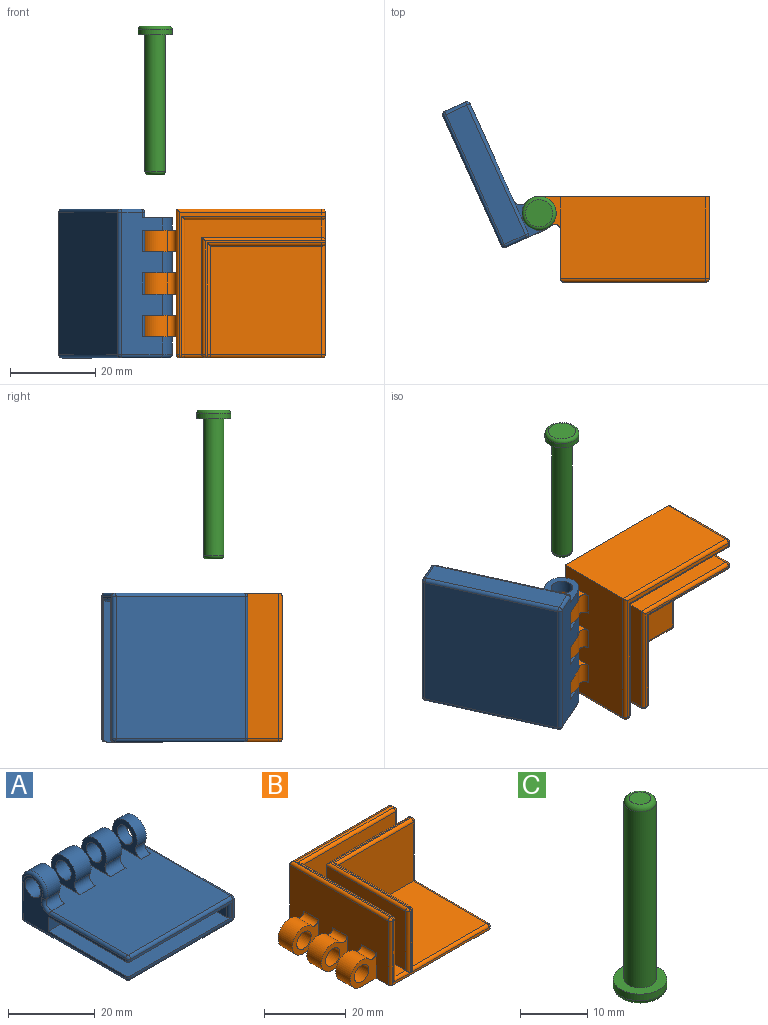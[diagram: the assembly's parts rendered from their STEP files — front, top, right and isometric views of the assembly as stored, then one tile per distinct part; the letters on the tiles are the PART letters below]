
ASSEMBLY  parts=3 mates=2
PART A: 55 faces, bbox 35x35.3x15.5 mm
  f0: plane 33.4x5.4mm, normal (1,0,0), area 180.4mm2, adj f42,f43,f47,f48
  f1: plane 33.4x10.4mm, normal (0,1,0), area 266.4mm2, adj f2,f3,f4,f5,f19,f20,f21,f23
  f2: cylinder r=4mm len=8mm, axis (1,0,0), area 71.1mm2, adj f1,f6,f23,f27
  f3: cylinder r=4mm len=8mm, axis (1,0,0), area 71.1mm2, adj f1,f7,f20,f24
  f4: cylinder r=4mm len=8mm, axis (1,0,0), area 42.7mm2, adj f1,f8,f19,f21
  f5: cylinder r=4mm len=8mm, axis (1,0,0), area 59.7mm2, adj f1,f9,f26,f30
  f6: cylinder r=1.84mm len=5mm, axis (1,0,0), area 18.3mm2, adj f2,f18,f23,f27
  f7: cylinder r=1.84mm len=5mm, axis (1,0,0), area 18.3mm2, adj f3,f18,f20,f24
  f8: cylinder r=1.84mm len=3mm, axis (1,0,0), area 11mm2, adj f4,f18,f19,f21
  f9: cylinder r=1.84mm len=4.2mm, axis (1,0,0), area 15.4mm2, adj f5,f18,f26,f32
  f10: cylinder r=2.5mm len=5mm, axis (1,0,0), area 78.5mm2, adj f12,f26
  f11: plane 33.8x26mm, normal (0,0,1), area 858mm2, adj f12,f13,f15,f16,f29,f54
  f12: plane 33.4x13.6mm, normal (-1,0,0), area 107.6mm2, adj f10,f11,f15,f17,f29,f30,f32,f33
  f13: plane 33.4x5.4mm, normal (0,-1,0), area 48.4mm2, adj f11,f17,f29,f35,f36,f43,f44,f54
  f14: plane 33.4x33.4mm, normal (0,0,-1), area 1115.6mm2, adj f34,f35,f41,f42
  f15: plane 33x4mm, normal (0,-1,0), area 132mm2, adj f11,f12,f16,f17
  f16: plane 25.2x4mm, normal (-1,0,0), area 100.8mm2, adj f11,f15,f17,f54
  f17: plane 33.8x26mm, normal (0,0,-1), area 858mm2, adj f12,f13,f15,f16,f36,f54
  f18: plane 33.4x33.4mm, normal (0,0,1), area 968.5mm2, adj f6,f7,f8,f9,f19,f20,f21,f23
  f19: plane 9.35x9mm, normal (1,0,0), area 38.5mm2, adj f1,f4,f8,f18,f28,f50
  f20: plane 9.35x9mm, normal (1,0,0), area 38.5mm2, adj f1,f3,f7,f18,f22,f51
  f21: plane 9.35x9mm, normal (-1,0,0), area 38.5mm2, adj f1,f4,f8,f18,f28,f51
  f22: cylinder r=2.5mm len=5mm, axis (1,0,0), area 78.5mm2, adj f20,f24
  f23: plane 9.35x9mm, normal (1,0,0), area 38.5mm2, adj f1,f2,f6,f18,f25,f52
  f24: plane 9.35x9mm, normal (-1,0,0), area 38.5mm2, adj f1,f3,f7,f18,f22,f52
  f25: cylinder r=2.5mm len=5mm, axis (1,0,0), area 78.5mm2, adj f23,f27
  f26: plane 9.35x9mm, normal (1,0,0), area 38.5mm2, adj f1,f5,f9,f10,f18,f53
  f27: plane 9.35x9mm, normal (-1,0,0), area 38.5mm2, adj f1,f2,f6,f18,f25,f53
  f28: cylinder r=2.5mm len=5mm, axis (1,0,0), area 47.1mm2, adj f19,f21
  f29: cylinder r=0.8mm len=0.8mm, axis (0,0,1), area 0.9mm2, adj f11,f12,f13,f31
  f30: torus R=3.2mm, axis (1,0,0), area 16.6mm2, adj f5,f12,f32,f33
  f31: sphere r=0.8mm, area 1mm2, adj f29,f34,f35
  f32: torus R=2.64mm, axis (1,0,0), area 5.3mm2, adj f9,f12,f30,f37
  f33: cylinder r=0.8mm len=10.4mm, axis (0,0,-1), area 13.1mm2, adj f1,f12,f30,f38
  f34: cylinder r=0.8mm len=33.4mm, axis (0,-1,0), area 42mm2, adj f12,f14,f31,f38
  f35: cylinder r=0.8mm len=33.4mm, axis (1,0,0), area 42mm2, adj f13,f14,f31,f39
  f36: cylinder r=0.8mm len=0.8mm, axis (0,0,1), area 0.9mm2, adj f12,f13,f17,f40
  f37: cylinder r=0.8mm len=24.85mm, axis (0,1,0), area 31.2mm2, adj f12,f18,f32,f40
  f38: sphere r=0.8mm, area 1mm2, adj f33,f34,f41
  f39: sphere r=0.8mm, area 1mm2, adj f35,f42,f43
  f40: sphere r=0.8mm, area 1mm2, adj f36,f37,f44
  f41: cylinder r=0.8mm len=33.4mm, axis (-1,0,0), area 42mm2, adj f1,f14,f38,f45
  f42: cylinder r=0.8mm len=33.4mm, axis (0,1,0), area 42mm2, adj f0,f14,f39,f45
  f43: cylinder r=0.8mm len=5.4mm, axis (0,0,-1), area 6.8mm2, adj f0,f13,f39,f46
  f44: cylinder r=0.8mm len=33.4mm, axis (-1,0,0), area 42mm2, adj f13,f18,f40,f46
  f45: sphere r=0.8mm, area 1mm2, adj f41,f42,f47
  f46: sphere r=0.8mm, area 1mm2, adj f43,f44,f48
  f47: cylinder r=0.8mm len=5.4mm, axis (0,0,1), area 6.8mm2, adj f0,f1,f45,f49
  f48: cylinder r=0.8mm len=33.4mm, axis (0,-1,0), area 42mm2, adj f0,f18,f46,f49
  f49: sphere r=0.8mm, area 1mm2, adj f47,f48,f50
  f50: cylinder r=0.8mm len=1.2mm, axis (1,0,0), area 1.5mm2, adj f1,f18,f19,f49
  f51: cylinder r=0.8mm len=5mm, axis (1,0,0), area 6.3mm2, adj f1,f18,f20,f21
  f52: cylinder r=0.8mm len=5mm, axis (1,0,0), area 6.3mm2, adj f1,f18,f23,f24
  f53: cylinder r=0.8mm len=5mm, axis (1,0,0), area 6.3mm2, adj f1,f18,f26,f27
  f54: cylinder r=0.8mm len=4mm, axis (0,0,1), area 5mm2, adj f11,f13,f16,f17
PART B: 64 faces, bbox 44x35x20 mm
  f0: plane 40.77x35mm, normal (0,0,-1), area 1311.2mm2, adj f4,f5,f6,f7,f9,f10,f11,f21
  f1: cylinder r=1.28mm len=5mm, axis (0,1,0), area 15mm2, adj f4,f7,f24,f26
  f2: cylinder r=1.28mm len=5mm, axis (0,1,0), area 15mm2, adj f5,f7,f22,f25
  f3: cylinder r=1.28mm len=5mm, axis (0,1,0), area 15mm2, adj f6,f7,f21,f23
  f4: cylinder r=4mm len=7.92mm, axis (0,1,0), area 74.6mm2, adj f0,f1,f24,f26
  f5: cylinder r=4mm len=7.92mm, axis (0,1,0), area 74.6mm2, adj f0,f2,f22,f25
  f6: cylinder r=4mm len=7.92mm, axis (0,1,0), area 74.6mm2, adj f0,f3,f21,f23
  f7: plane 34.2x19.2mm, normal (-1,0,0), area 541.7mm2, adj f0,f1,f2,f3,f11,f21,f22,f23
  f8: plane 32.2x31.7mm, normal (0,0,1), area 245.2mm2, adj f13,f14,f16,f17,f43,f47
  f9: plane 33.4x19.2mm, normal (0,-1,0), area 38.2mm2, adj f0,f30,f35,f41,f43,f45,f51,f57
  f10: plane 33.4x19.2mm, normal (1,0,0), area 47.4mm2, adj f0,f34,f40,f44,f47,f50,f56,f59
  f11: plane 34.2x19.2mm, normal (0,1,0), area 656.6mm2, adj f0,f7,f33,f34
  f12: plane 26.2x25.5mm, normal (0,0,1), area 668.1mm2, adj f18,f19,f60,f63
  f13: plane 31.7x17.7mm, normal (1,0,0), area 561.1mm2, adj f8,f14,f36,f41
  f14: plane 32.2x17.7mm, normal (0,-1,0), area 569.9mm2, adj f8,f13,f39,f44
  f15: plane 33.4x33.4mm, normal (0,0,1), area 43.1mm2, adj f31,f33,f35,f36,f39,f40
  f16: plane 28.2x17.7mm, normal (0,1,0), area 499.1mm2, adj f8,f17,f49,f50
  f17: plane 27.5x17.7mm, normal (-1,0,0), area 486.7mm2, adj f8,f16,f45,f46
  f18: plane 25.5x17.7mm, normal (1,0,0), area 451.3mm2, adj f12,f19,f52,f57
  f19: plane 26.2x17.7mm, normal (0,-1,0), area 463.7mm2, adj f12,f18,f55,f61
  f20: plane 27.4x26.7mm, normal (0,0,1), area 21.5mm2, adj f46,f49,f51,f52,f55,f56
  f21: plane 9x7.92mm, normal (0,-1,0), area 41.2mm2, adj f0,f3,f6,f7,f27
  f22: plane 9x7.92mm, normal (0,-1,0), area 41.2mm2, adj f0,f2,f5,f7,f28
  f23: plane 9x7.92mm, normal (0,1,0), area 41.2mm2, adj f0,f3,f6,f7,f27
  f24: plane 9x7.92mm, normal (0,-1,0), area 41.2mm2, adj f0,f1,f4,f7,f29
  f25: plane 9x7.92mm, normal (0,1,0), area 41.2mm2, adj f0,f2,f5,f7,f28
  f26: plane 9x7.92mm, normal (0,1,0), area 41.2mm2, adj f0,f1,f4,f7,f29
  f27: cylinder r=2.5mm len=5mm, axis (0,1,0), area 78.5mm2, adj f21,f23
  f28: cylinder r=2.5mm len=5mm, axis (0,1,0), area 78.5mm2, adj f22,f25
  f29: cylinder r=2.5mm len=5mm, axis (0,1,0), area 78.5mm2, adj f24,f26
  f30: cylinder r=0.8mm len=19.2mm, axis (0,0,-1), area 24.1mm2, adj f0,f7,f9,f32
  f31: cylinder r=0.8mm len=34.2mm, axis (0,1,0), area 42.6mm2, adj f7,f15,f32,f33
  f32: sphere r=0.8mm, area 1mm2, adj f30,f31,f35
  f33: cylinder r=0.8mm len=34.2mm, axis (1,0,0), area 42.6mm2, adj f11,f15,f31,f37
  f34: cylinder r=0.8mm len=19.2mm, axis (0,0,-1), area 24.1mm2, adj f0,f10,f11,f37
  f35: cylinder r=0.8mm len=0.8mm, axis (-1,0,0), area 0.5mm2, adj f9,f15,f32,f38
  f36: cylinder r=0.8mm len=32.5mm, axis (0,-1,0), area 40.2mm2, adj f13,f15,f38,f39
  f37: sphere r=0.8mm, area 1mm2, adj f33,f34,f40
  f38: sphere r=0.8mm, area 1mm2, adj f35,f36,f41
  f39: cylinder r=0.8mm len=33mm, axis (-1,0,0), area 40.8mm2, adj f14,f15,f36,f42
  f40: cylinder r=0.8mm len=0.9mm, axis (0,-1,0), area 1.1mm2, adj f10,f15,f37,f42
  f41: cylinder r=0.8mm len=18.5mm, axis (0,0,1), area 22.6mm2, adj f9,f13,f38,f43
  f42: sphere r=0.8mm, area 1mm2, adj f39,f40,f44
  f43: cylinder r=0.8mm len=5.6mm, axis (-1,0,0), area 5.8mm2, adj f8,f9,f41,f45
  f44: cylinder r=0.8mm len=18.5mm, axis (0,0,1), area 22.6mm2, adj f10,f14,f42,f47
  f45: cylinder r=0.8mm len=18.5mm, axis (0,0,-1), area 22.6mm2, adj f9,f17,f43,f48
  f46: cylinder r=0.8mm len=27.5mm, axis (0,1,0), area 34.2mm2, adj f17,f20,f48,f49
  f47: cylinder r=0.8mm len=5.8mm, axis (0,-1,0), area 6mm2, adj f8,f10,f44,f50
  f48: sphere r=0.8mm, area 1mm2, adj f45,f46,f51
  f49: cylinder r=0.8mm len=28.2mm, axis (1,0,0), area 35.1mm2, adj f16,f20,f46,f53
  f50: cylinder r=0.8mm len=18.5mm, axis (0,0,-1), area 22.6mm2, adj f10,f16,f47,f53
  f51: cylinder r=0.8mm len=0.8mm, axis (-1,0,0), area 0.5mm2, adj f9,f20,f48,f54
  f52: cylinder r=0.8mm len=26.3mm, axis (0,-1,0), area 32.4mm2, adj f18,f20,f54,f55
  f53: sphere r=0.8mm, area 1mm2, adj f49,f50,f56
  f54: sphere r=0.8mm, area 1mm2, adj f51,f52,f57
  f55: cylinder r=0.8mm len=27mm, axis (-1,0,0), area 33.3mm2, adj f19,f20,f52,f58
  f56: cylinder r=0.8mm len=0.8mm, axis (0,-1,0), area 0.5mm2, adj f10,f20,f53,f58
  f57: cylinder r=0.8mm len=18.5mm, axis (0,0,1), area 22.6mm2, adj f9,f18,f54,f60
  f58: sphere r=0.8mm, area 1mm2, adj f55,f56,f61
  f59: cylinder r=0.8mm len=0.8mm, axis (0,0,1), area 0.9mm2, adj f0,f9,f10,f62
  f60: cylinder r=0.8mm len=27mm, axis (-1,0,0), area 33.3mm2, adj f9,f12,f57,f62
  f61: cylinder r=0.8mm len=18.5mm, axis (0,0,1), area 22.6mm2, adj f10,f19,f58,f63
  f62: sphere r=0.8mm, area 1mm2, adj f59,f60,f63
  f63: cylinder r=0.8mm len=26.3mm, axis (0,-1,0), area 32.4mm2, adj f10,f12,f61,f62
PART C: 7 faces, bbox 8.7x8.7x35 mm
  f0: cylinder r=4mm len=8mm, axis (0,0,-1), area 30.2mm2, adj f1,f6
  f1: plane 8x8mm, normal (0,0,1), area 32.2mm2, adj f0,f3
  f2: plane 6.4x6.4mm, normal (0,0,-1), area 32.2mm2, adj f6
  f3: cylinder r=2.4mm len=32.2mm, axis (0,0,-1), area 485.6mm2, adj f1,f5
  f4: plane 3.2x3.2mm, normal (0,0,1), area 8mm2, adj f5
  f5: torus R=1.6mm, axis (0,0,1), area 16.7mm2, adj f3,f4
  f6: torus R=3.2mm, axis (0,0,1), area 29.3mm2, adj f0,f2
PLACE A rot(axis=(-0.7,-0.15,-0.7),162.9deg) t=(-28.59,36.24,48.84)mm
PLACE B rot(axis=(1,0,0),90deg) t=(-13.84,3.92,-18.78)mm
PLACE C rot(axis=(-0.21,0.98,0),180deg) t=(-7.74,-81.46,73)mm
MATE revolute B.f4 <-> A.f2  axis (0,0,1) through (0,0,25)mm
MATE slider C.f0 <-> A.f2  axis (0,0,-1) through (0,0,38)mm
